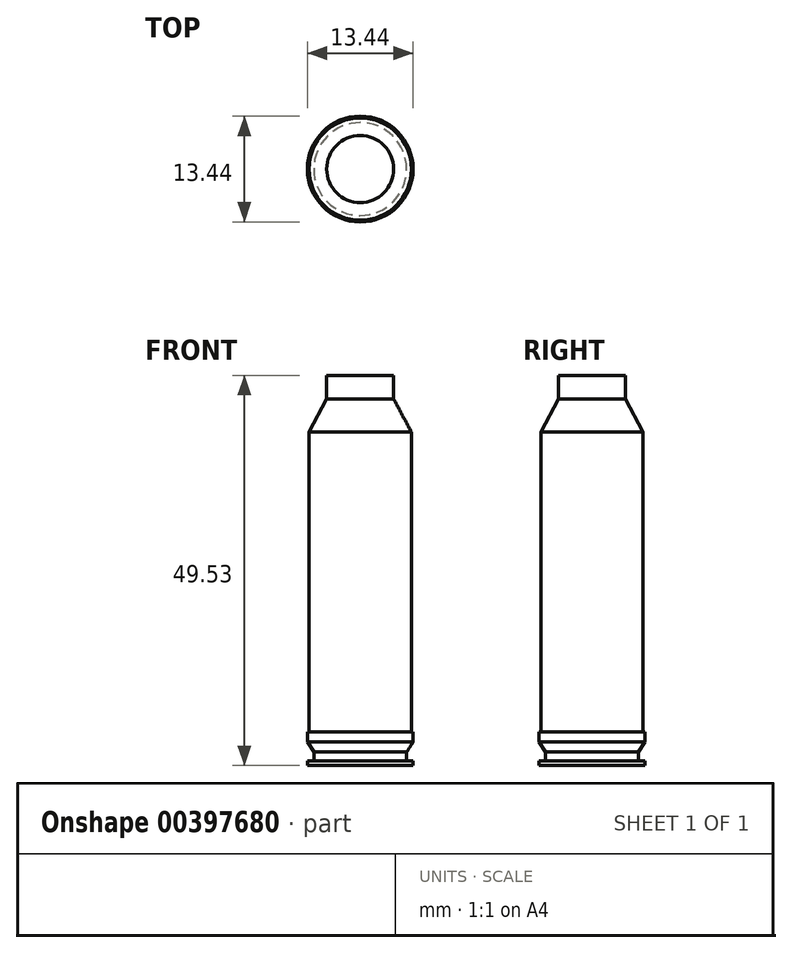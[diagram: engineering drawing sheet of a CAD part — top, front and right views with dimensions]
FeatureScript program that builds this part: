
annotation { "Feature Type Name" : "Feature", "Feature Type Description" : "" }
export const myFeature = defineFeature(function(context is Context, id is Id, definition is map)
    precondition{}
    {
        {
            var Q0;
            Q0=qCreatedBy(makeId("Front.planeOp"),FACE);
            var sketch = newSketch(context, id + "F0", { "sketchPlane" : qUnion([Q0])});
            skLineSegment(sketch, "E0", {"start": v(0, -27.25) * mm, "end": v(6.72, -27.25) * mm});
            skLineSegment(sketch, "E1", {"start": v(6.72, -27.25) * mm, "end": v(6.72, -26.65) * mm});
            skLineSegment(sketch, "E2", {"start": v(6.72, -26.65) * mm, "end": v(5.9, -26.65) * mm});
            skLineSegment(sketch, "E3", {"start": v(5.9, -26.65) * mm, "end": v(5.9, -25.56) * mm});
            skLineSegment(sketch, "E4", {"start": v(5.9, -25.56) * mm, "end": v(6.72, -24.28) * mm});
            skLineSegment(sketch, "E5", {"start": v(6.72, -24.28) * mm, "end": v(6.72, -23.01) * mm});
            skLineSegment(sketch, "E6", {"start": v(6.72, -23.01) * mm, "end": v(6.5, -23.01) * mm});
            skLineSegment(sketch, "E7", {"start": v(6.5, -23.01) * mm, "end": v(6.5, 15.09) * mm});
            skLineSegment(sketch, "E8", {"start": v(6.5, 15.09) * mm, "end": v(4.25, 19.27) * mm});
            skLineSegment(sketch, "E9", {"start": v(4.25, 19.27) * mm, "end": v(4.25, 22.28) * mm});
            skLineSegment(sketch, "E10", {"start": v(4.25, 22.28) * mm, "end": v(0, 22.28) * mm});
            skLineSegment(sketch, "E11", {"start": v(0, 22.28) * mm, "end": v(0, -27.25) * mm});
            skSolve(sketch);
        }
        {
            var Q0;
            Q0=makeQuery(id+"F0.imprint","IMPRINT",FACE,{"disambiguationData":[TD([[makeQuery(id+"F0.imprint","IMPRINT",EDGE,{"derivedFrom":sQuery(id+"F0.wireOp",EDGE,"E0")}),1.0]])]});
            var Q1;
            Q1=sQuery(id+"F0.wireOp",EDGE,"E11");
            revolve(context, id + "F1", {"entities" : qUnion([Q0]), "axis" : qUnion([Q1]), "revolveType" : RevolveType.FULL});
        }
    });
